# Revit family: Zumtobel TECTON C
name_source: partatom
category: Lighting Fixtures
revit_build: Autodesk Revit 2014 (Build: 20130308_1515(x64)
units: mm (PartAtom-declared; Revit-internal decimal feet)

## types (9) — shared parameters
Apparent Load = 0 VA
Assembly Code = D5020210
Default Elevation = 1219 mm
Description = LED continuous-row luminaire
Manufacturer = Zumtobel Lighting
URL = http://www.zumtobel.com
zero-valued in all types: Versatz

## per-type parameters (varying)
| type | Fixture Type | Length |
| TECTON C LED L1000 | Zumtobel TECTON C (Lamp & Reflector) : TECTON C LED L1000 | 1000 mm  [stored 3.28084 ft] |
| TECTON C LED L1500 | Zumtobel TECTON C (Lamp & Reflector) : TECTON C LED L1500 | 1498 mm  [stored 4.9147 ft] |
| TECTON C LED L2000 | Zumtobel TECTON C (Lamp & Reflector) : TECTON C LED L2000 | 1997 mm  [stored 6.55184 ft] |
| TECTON C LED L2000 WW | Zumtobel TECTON C (Lamp & Reflector) : TECTON C LED L2000 WW | 1997 mm  [stored 6.55184 ft] |
| TECTON C LED L1000 WW | Zumtobel TECTON C (Lamp & Reflector) : TECTON C LED L1000 WW | 1000 mm  [stored 3.28084 ft] |
| TECTON C LED L1500 WW | Zumtobel TECTON C (Lamp & Reflector) : TECTON C LED L1500 WW | 1498 mm  [stored 4.9147 ft] |
| TECTON C LED L1000 + CG | Zumtobel TECTON C (Lamp & Reflector) : TECTON C LED L1000 + CG | 1000 mm  [stored 3.28084 ft] |
| TECTON C LED L1500 + CG | Zumtobel TECTON C (Lamp & Reflector) : TECTON C LED L1500 + CG | 1498 mm  [stored 4.9147 ft] |
| TECTON C LED L2000 + CG | Zumtobel TECTON C (Lamp & Reflector) : TECTON C LED L2000 + CG | 1997 mm  [stored 6.55184 ft] |

note: [stored X ft] marks values corroborated as IEEE doubles in the binary element streams (Revit-internal decimal feet)

## geometry (parser evidence)
native form markers: Blend x24, Sweep x5
no freeform markers — native parametric forms only
